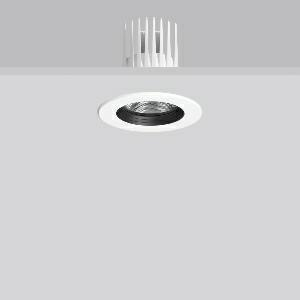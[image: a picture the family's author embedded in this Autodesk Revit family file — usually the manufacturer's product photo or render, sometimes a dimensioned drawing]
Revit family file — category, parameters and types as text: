
# Revit family: heledon_mini_e_901742_002_1_89b6
name_source: partatom
category: Lighting Fixtures
units: mm (PartAtom-declared; Revit-internal decimal feet)

## family parameters
Cut with Voids When Loaded = No
Host = Face
Light Source = No
Part Type = Normal
Room Calculation Point = No
Round Connector Dimension = Use Diameter
Shared = No

## types (1)
- HELEDON mini E (1 x LED Modul 940, 2750 lm, 4000)
    Apparent Load = 20 VA
    Approval mark = CE
    CIE Flux Codes = 95 99 100 100 100
    Color Rendering = 92
    Color Temperature = 4000
    Default Elevation = 1800 mm
    Description = Series: HELEDON mini
Round recessed downlight. Housing: die-cast aluminium, powder-coated. Black plastic ring and recessed LED to prevent glare from the side. Optical assembly with reflector made of MIRO-Silver with 98% total light reflection for outstanding efficiency - can be changed without tools. Best colour rendering index Ra>90. Suitable for Recessed ceiling mounting. Installation without tools thanks to spring fastening system. Including separate LED converter with connecting cable 600 mm.High quality converter without flickering and stroboscopic effect. Through-wiring box (5 pole) available as accessory. The following accessories can be mounted without use of tools: interchangeable lenses, decorative glasses, honeycomb louvre, clear and frosted diffusers, white interchangeable plastic ring. 
Colour: traffic white, matt (RAL 9016)
Diameter: 124 mm
Height: 3 mm
Cut-out diameter: 114 mm
Recess height: 170 mm
Luminaire: recess height: 120 mm
Lamp: LED
Socket: without socket
Colour temperature: 4000K
Colour rendering index (CRI): 92
System power: 20 W
Rated luminous flux: 2750 lm
Luminous efficiency: 138 lm/W
Control gear: Regulated power supply
Protection class: II
Type of protection: IP 20
    Height = 0 mm  [stored 0 ft]
    Lamp = 1 x LED Modul 940
    Lamp Light Flux = 2750 lm
    Lamp count = 1
    Length = 124 mm  [stored 0.406824 ft]
    Lifetime = 50000 h
    Luminous efficacy = 138 lm/W
    Manufacturer = RZB
    ModVariant = No
    Model = 901742.002.1
    Mounting Place = Ceiling
    Mounting Type = Recessed
    Number of Poles = 1
    OnlyDefault = Yes
    Power Factor = 1
    Product Name = HELEDON mini E
    Product group = Recessed downlights
    ProductGroupID = 402
    Protection Class = Protection class II
    Protection Degree = IP 20
    RLX_Detail_Level = 1
    RLX_Emergency_Light_Flux = 0 lm
    RLX_Emergency_Type = 0
    RLX_Emergency_Type_DB = No
    RlxData = <blob elided: 125933 chars, md5=ae8545b4>
    Socket = socket
    Standby Power = 0 W
    System Light Flux = 2750 lm
    System Power = 20 W
    Type Comments = Product without accessories
    Type Image = 901657.002.jpg
    URL = http://relux.com
    VarID = ---
    Voltage = 230 V
    Voltage Range = 220-240 V
    Weight = 0.00 kg
    Width = 0 mm  [stored 0 ft]

note: [stored X ft] marks values corroborated as IEEE doubles in the binary element streams (Revit-internal decimal feet)

## geometry (parser evidence)
native form markers: Blend x4, Sweep x12
no freeform markers — native parametric forms only
